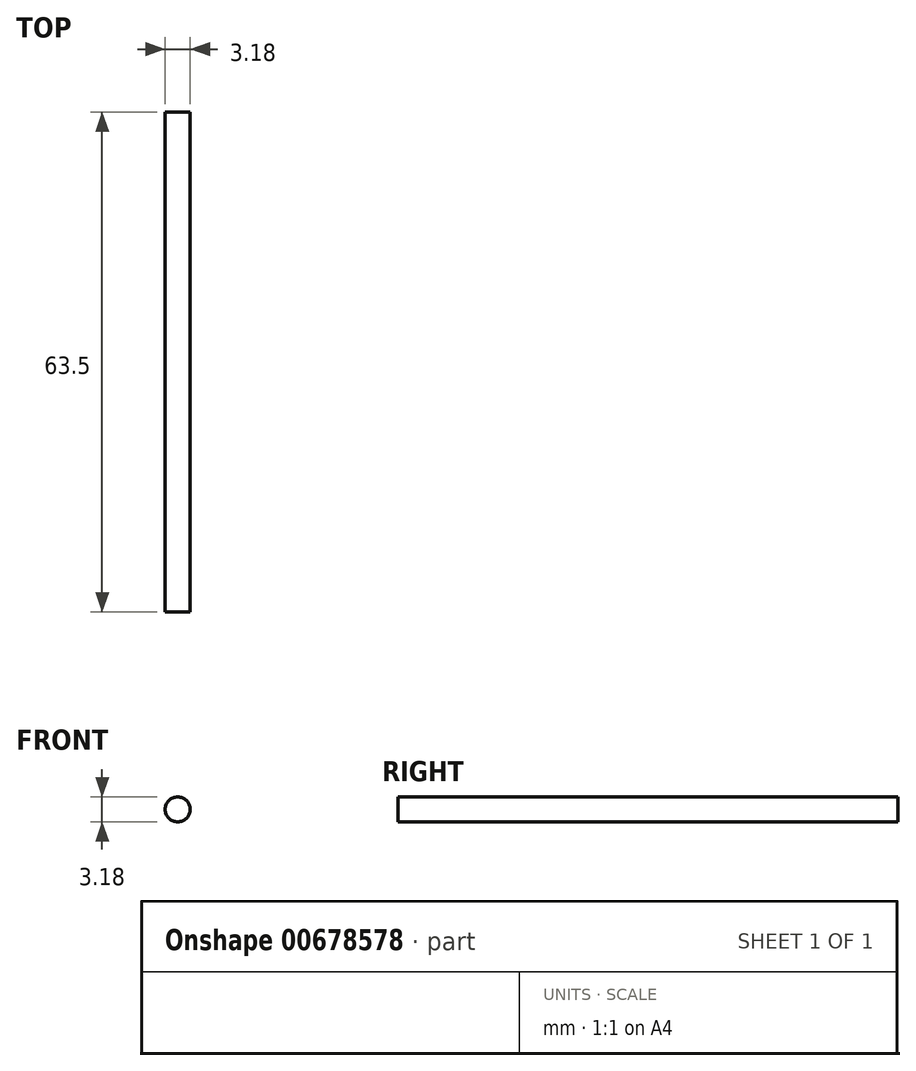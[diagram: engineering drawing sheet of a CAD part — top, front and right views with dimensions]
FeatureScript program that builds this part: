
annotation { "Feature Type Name" : "Feature", "Feature Type Description" : "" }
export const myFeature = defineFeature(function(context is Context, id is Id, definition is map)
    precondition{}
    {
        {
            var Q0;
            Q0=qCreatedBy(makeId("Front.planeOp"),FACE);
            var sketch = newSketch(context, id + "F0", { "sketchPlane" : qUnion([Q0])});
            skCircle(sketch, "E0", {"center": v(0, 0) * mm, "radius": 1.59 * mm});
            skSolve(sketch);
        }
        {
            var Q0;
            Q0 = qSketchRegion(id + "F0", true);
            extrude(context, id + "F1", {"entities" : qUnion([Q0]), "depth" : 63.5 * mm, "offsetDistance" : 25.4 * mm});
        }
    });
